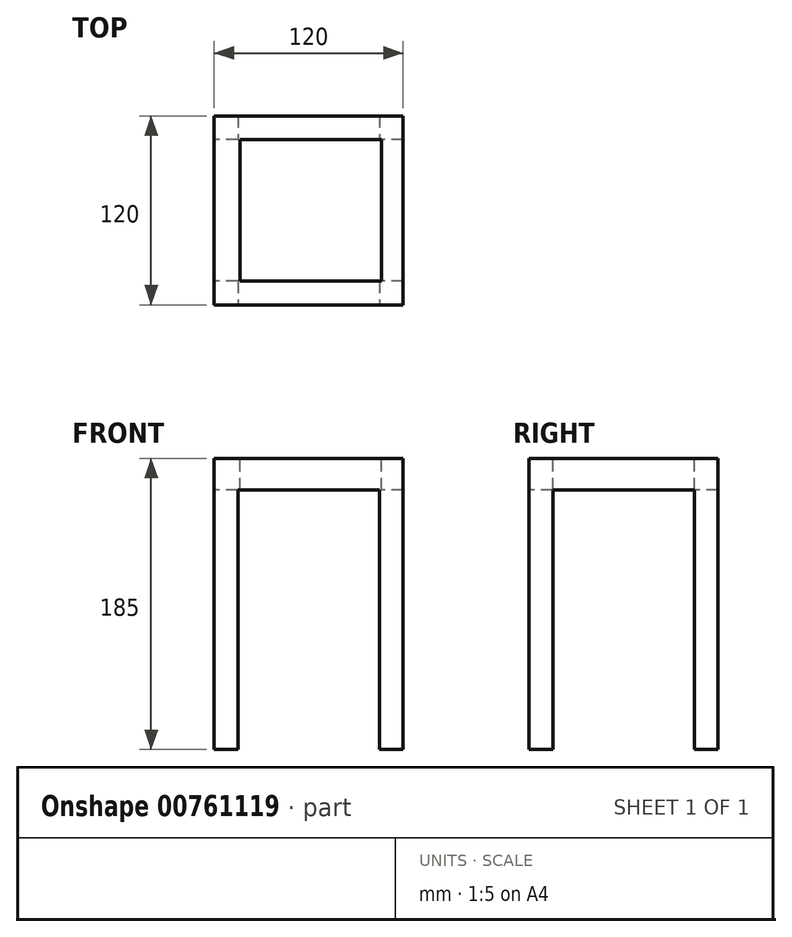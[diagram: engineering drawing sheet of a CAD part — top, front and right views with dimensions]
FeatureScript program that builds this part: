
annotation { "Feature Type Name" : "Feature", "Feature Type Description" : "" }
export const myFeature = defineFeature(function(context is Context, id is Id, definition is map)
    precondition{}
    {
        {
            var Q0;
            Q0=qCreatedBy(makeId("Top.planeOp"),FACE);
            var sketch = newSketch(context, id + "F0", { "sketchPlane" : qUnion([Q0])});
            skLineSegment(sketch, "E0.bottom", {"start": v(-60.62, 87.3) * mm, "end": v(59.38, 87.3) * mm});
            skLineSegment(sketch, "E0.top", {"start": v(-60.62, -32.7) * mm, "end": v(59.38, -32.7) * mm});
            skLineSegment(sketch, "E0.left", {"start": v(-60.62, 87.3) * mm, "end": v(-60.62, -32.7) * mm});
            skLineSegment(sketch, "E0.right", {"start": v(59.38, 87.3) * mm, "end": v(59.38, -32.7) * mm});
            skSolve(sketch);
        }
        {
            var Q0;
            Q0 = qSketchRegion(id + "F0", true);
            extrude(context, id + "F1", {"entities" : qUnion([Q0]), "depth" : 5 * mm, "offsetDistance" : 25 * mm});
        }
        {
            var Q0;
            Q0=makeQuery(id+"F1.opExtrude","CAP_FACE",FACE,{"disambiguationData":[OSD([sQuery(id+"F0.wireOp",EDGE,"E0.bottom"),sQuery(id+"F0.wireOp",EDGE,"E0.top"),sQuery(id+"F0.wireOp",EDGE,"E0.left"),sQuery(id+"F0.wireOp",EDGE,"E0.right")])],"isStart":false});
            var sketch = newSketch(context, id + "F2", { "sketchPlane" : qUnion([Q0])});
            skCircle(sketch, "E1", {"center": v(-0.62, 27.3) * mm, "radius": 12.5 * mm});
            skPoint(sketch, "E1.centerSnap0", {"position": v(-60.62, 27.3) * mm});
            skPoint(sketch, "E1.centerSnap1", {"position": v(-0.62, 87.3) * mm});
            skSolve(sketch);
        }
        {
            var Q0;
            Q0 = qSketchRegion(id + "F2", true);
            extrude(context, id + "F3", {"entities" : qUnion([Q0]), "operationType" : NewBodyOperationType.REMOVE, "oppositeDirection" : true, "depth" : 25 * mm, "offsetDistance" : 25 * mm});
        }
        {
            var Q0;
            Q0=makeQuery(id+"F1.opExtrude","CAP_FACE",FACE,{"disambiguationData":[OSD([sQuery(id+"F0.wireOp",EDGE,"E0.bottom"),sQuery(id+"F0.wireOp",EDGE,"E0.top"),sQuery(id+"F0.wireOp",EDGE,"E0.left"),sQuery(id+"F0.wireOp",EDGE,"E0.right")])],"isStart":false});
            var sketch = newSketch(context, id + "F4", { "sketchPlane" : qUnion([Q0])});
            skLineSegment(sketch, "E2.bottom", {"start": v(-60.62, -32.7) * mm, "end": v(59.38, -32.7) * mm});
            skLineSegment(sketch, "E2.top", {"start": v(-60.62, 87.3) * mm, "end": v(59.38, 87.3) * mm});
            skLineSegment(sketch, "E2.left", {"start": v(-60.62, -32.7) * mm, "end": v(-60.62, 87.3) * mm});
            skLineSegment(sketch, "E2.right", {"start": v(59.38, -32.7) * mm, "end": v(59.38, 87.3) * mm});
            skSolve(sketch);
        }
        {
            var Q0;
            Q0 = qSketchRegion(id + "F4", true);
            extrude(context, id + "F5", {"entities" : qUnion([Q0]), "operationType" : NewBodyOperationType.ADD, "depth" : 180 * mm, "offsetDistance" : 25 * mm});
        }
        {
            var Q0;
            Q0=makeQuery(id+"F5.boolean.opBoolean","MERGE",FACE,{"derivedFrom":[makeQuery(id+"F1.opExtrude","SWEPT_FACE",FACE,{"disambiguationData":[OSD([sQuery(id+"F0.wireOp",EDGE,"E0.top")])]}),makeQuery(id+"F5.opExtrude","SWEPT_FACE",FACE,{"disambiguationData":[OSD([sQuery(id+"F4.wireOp",EDGE,"E2.bottom")])]})]});
            var sketch = newSketch(context, id + "F6", { "sketchPlane" : qUnion([Q0])});
            skLineSegment(sketch, "E3.bottom", {"start": v(-45.62, 165) * mm, "end": v(44.38, 165) * mm});
            skLineSegment(sketch, "E3.top", {"start": v(-45.62, 0) * mm, "end": v(44.38, 0) * mm});
            skLineSegment(sketch, "E3.left", {"start": v(-45.62, 165) * mm, "end": v(-45.62, 0) * mm});
            skLineSegment(sketch, "E3.right", {"start": v(44.38, 165) * mm, "end": v(44.38, 0) * mm});
            skSolve(sketch);
        }
        {
            var Q0;
            Q0 = qSketchRegion(id + "F6", true);
            extrude(context, id + "F7", {"entities" : qUnion([Q0]), "operationType" : NewBodyOperationType.REMOVE, "oppositeDirection" : true, "depth" : 120 * mm, "offsetDistance" : 25 * mm});
        }
        {
            var Q0;
            Q0=makeQuery(id+"F5.boolean.opBoolean","MERGE",FACE,{"derivedFrom":[makeQuery(id+"F1.opExtrude","SWEPT_FACE",FACE,{"disambiguationData":[OSD([sQuery(id+"F0.wireOp",EDGE,"E0.left")])]}),makeQuery(id+"F5.opExtrude","SWEPT_FACE",FACE,{"disambiguationData":[OSD([sQuery(id+"F4.wireOp",EDGE,"E2.left")])]})]});
            var sketch = newSketch(context, id + "F8", { "sketchPlane" : qUnion([Q0])});
            skLineSegment(sketch, "E4.bottom", {"start": v(-72.3, 165) * mm, "end": v(17.7, 165) * mm});
            skLineSegment(sketch, "E4.top", {"start": v(-72.3, 0) * mm, "end": v(17.7, 0) * mm});
            skLineSegment(sketch, "E4.left", {"start": v(-72.3, 165) * mm, "end": v(-72.3, 0) * mm});
            skLineSegment(sketch, "E4.right", {"start": v(17.7, 165) * mm, "end": v(17.7, 0) * mm});
            skSolve(sketch);
        }
        {
            var Q0;
            Q0 = qSketchRegion(id + "F8", true);
            extrude(context, id + "F9", {"entities" : qUnion([Q0]), "operationType" : NewBodyOperationType.REMOVE, "oppositeDirection" : true, "depth" : 120 * mm, "offsetDistance" : 25 * mm});
        }
        {
            var Q0;
            Q0=makeQuery(id+"F5.opExtrude","CAP_FACE",FACE,{"disambiguationData":[OSD([sQuery(id+"F4.wireOp",EDGE,"E2.bottom"),sQuery(id+"F4.wireOp",EDGE,"E2.top"),sQuery(id+"F4.wireOp",EDGE,"E2.left"),sQuery(id+"F4.wireOp",EDGE,"E2.right")])],"isStart":false});
            var sketch = newSketch(context, id + "F10", { "sketchPlane" : qUnion([Q0])});
            skLineSegment(sketch, "E5.bottom", {"start": v(-44.35, 72.3) * mm, "end": v(45.65, 72.3) * mm});
            skLineSegment(sketch, "E5.top", {"start": v(-44.35, -17.7) * mm, "end": v(45.65, -17.7) * mm});
            skLineSegment(sketch, "E5.left", {"start": v(-44.35, 72.3) * mm, "end": v(-44.35, -17.7) * mm});
            skLineSegment(sketch, "E5.right", {"start": v(45.65, 72.3) * mm, "end": v(45.65, -17.7) * mm});
            skSolve(sketch);
        }
        {
            var Q0;
            Q0 = qSketchRegion(id + "F10", true);
            extrude(context, id + "F11", {"entities" : qUnion([Q0]), "operationType" : NewBodyOperationType.REMOVE, "oppositeDirection" : true, "depth" : 25 * mm, "offsetDistance" : 25 * mm});
        }
    });
